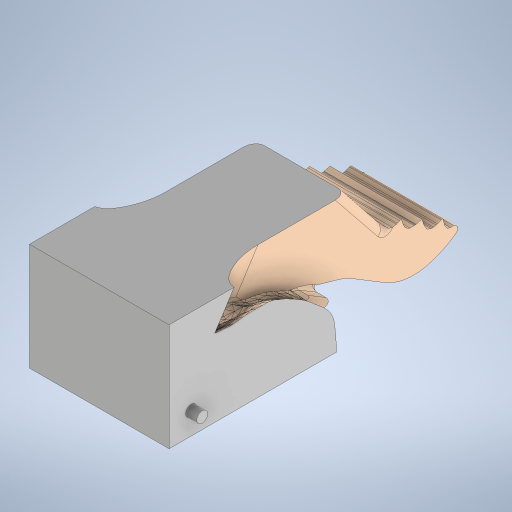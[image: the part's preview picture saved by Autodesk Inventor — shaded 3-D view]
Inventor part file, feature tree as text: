
AUTODESK INVENTOR PART (.ipt)
format: ipt  version: 2024 (Build 280153000, 153)  size: 11,114,496 bytes
history: native  units: mm
features: other x6, sketch x5, extrude x4, plane x2
ambient origin geometry x8: Origin, YZ Plane, XZ Plane, XY Plane, X Axis, Y Axis, Z Axis, Center Point
bodies: Body1 (feature_tree)
feature tree (17):
  other  "M.ipt"
  plane  "Plano de trabajo1"
  extrude  "Extrusión1"  [1 undecoded]
  other  "Combinar1"
  sketch  "Boceto3"  dims[d2=550.0mm d3=520.0mm]
  sketch  "Boceto4"  dims[d4=550.0mm d5=0.0mm d6=129.8482mm]
  plane  "Plano de trabajo2"
  sketch  "Boceto5"  dims[d17=180.0mm d18=180.0mm]
  extrude  "Extrusión2"  Depth=520.0mm
  extrude  "Extrusión5"  Depth=129.8482mm
  extrude  "Extrusión6"  Depth=180.0mm
  other  "Sólido1::M.ipt"
  other  "OperaciónIdentificador1"
  sketch  "Boceto1"  dims[d0=25.0mm d1=-365.0mm]
  other  "Sólido2"
  sketch  "Boceto7"  dims[d22=326.0mm d23=180.0mm d24=180.0mm d25=180.0mm d26=10.0mm d27=0.0mm d35=1000.0mm d36=0.0mm d37=30.0mm d38=30.0mm d39=15.0mm d40=15.0mm d41=205.0mm d42=0.0mm d43=0.0mm d14=0.5mm d15=0.872665mm d16=0.5mm d19=0.5mm d20=0.872665mm d21=0.5mm]
  other  "Sólido1"
note: 1 required parameter value undecoded (feature->parameter linkage not recoverable at this tier; creation-order binding heuristic only, values carry confidence <= 0.55)
